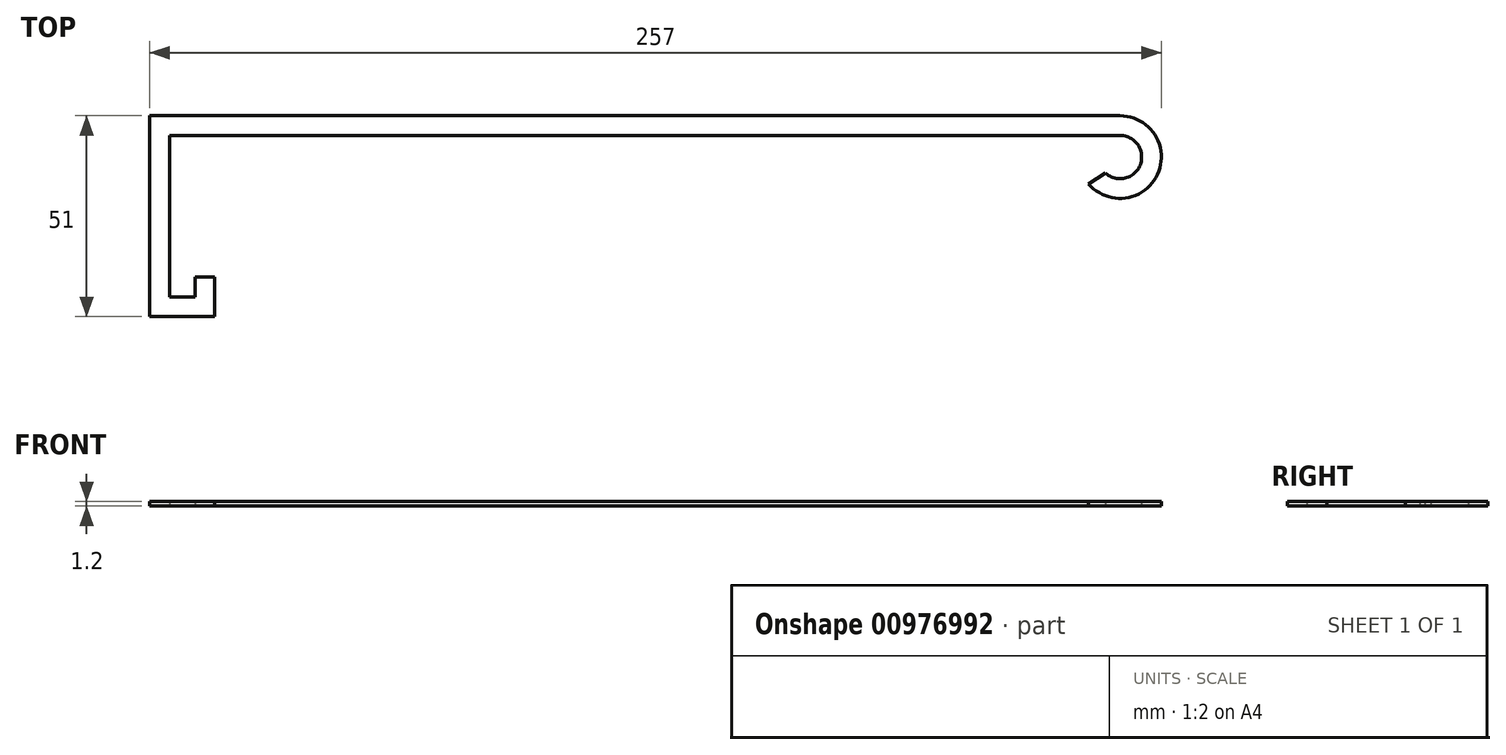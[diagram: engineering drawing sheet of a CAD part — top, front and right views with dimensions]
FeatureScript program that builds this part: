
annotation { "Feature Type Name" : "Feature", "Feature Type Description" : "" }
export const myFeature = defineFeature(function(context is Context, id is Id, definition is map)
    precondition{}
    {
        {
            var Q0;
            Q0=qCreatedBy(makeId("Top.planeOp"),FACE);
            var sketch = newSketch(context, id + "F0", { "sketchPlane" : qUnion([Q0])});
            skLineSegment(sketch, "E0", {"start": v(-201.26, 0) * mm, "end": v(-201.26, 51) * mm});
            skLineSegment(sketch, "E1", {"start": v(-201.26, 51) * mm, "end": v(-184.76, 51) * mm});
            skLineSegment(sketch, "E2", {"start": v(-201.26, 0) * mm, "end": v(-184.76, 0) * mm});
            skLineSegment(sketch, "E3", {"start": v(-184.76, 0) * mm, "end": v(-184.76, 10) * mm});
            skLineSegment(sketch, "E4", {"start": v(-184.76, 10) * mm, "end": v(-189.76, 10) * mm});
            skLineSegment(sketch, "E5", {"start": v(-189.76, 10) * mm, "end": v(-189.76, 5) * mm});
            skLineSegment(sketch, "E6", {"start": v(-189.76, 5) * mm, "end": v(-196.26, 5) * mm});
            skLineSegment(sketch, "E7", {"start": v(-196.26, 5) * mm, "end": v(-196.26, 46) * mm});
            skLineSegment(sketch, "E8", {"start": v(-196.26, 46) * mm, "end": v(-184.76, 46) * mm});
            skLineSegment(sketch, "E9", {"start": v(-184.76, 51) * mm, "end": v(45.24, 51) * mm});
            skLineSegment(sketch, "E10", {"start": v(-184.76, 46) * mm, "end": v(45.24, 46) * mm});
            skArc(sketch, "E11", {"start": v(37.24, 33.7) * mm, "mid": v(54.77, 36.1) * mm, "end": v(45.24, 51) * mm});
            skArc(sketch, "E12", {"start": v(41.56, 36.41) * mm, "mid": v(50.38, 38.53) * mm, "end": v(45.24, 46) * mm});
            skLineSegment(sketch, "E13", {"start": v(41.56, 36.41) * mm, "end": v(37.24, 33.7) * mm});
            skSolve(sketch);
        }
        {
            var Q0;
            Q0=makeQuery(id+"F0.imprint","IMPRINT",FACE,{"disambiguationData":[TD([[makeQuery(id+"F0.imprint","IMPRINT",EDGE,{"derivedFrom":sQuery(id+"F0.wireOp",EDGE,"E0")}),-1.0]])]});
            extrude(context, id + "F1", {"entities" : qUnion([Q0]), "depth" : 1.2 * mm, "offsetDistance" : 25 * mm});
        }
    });
